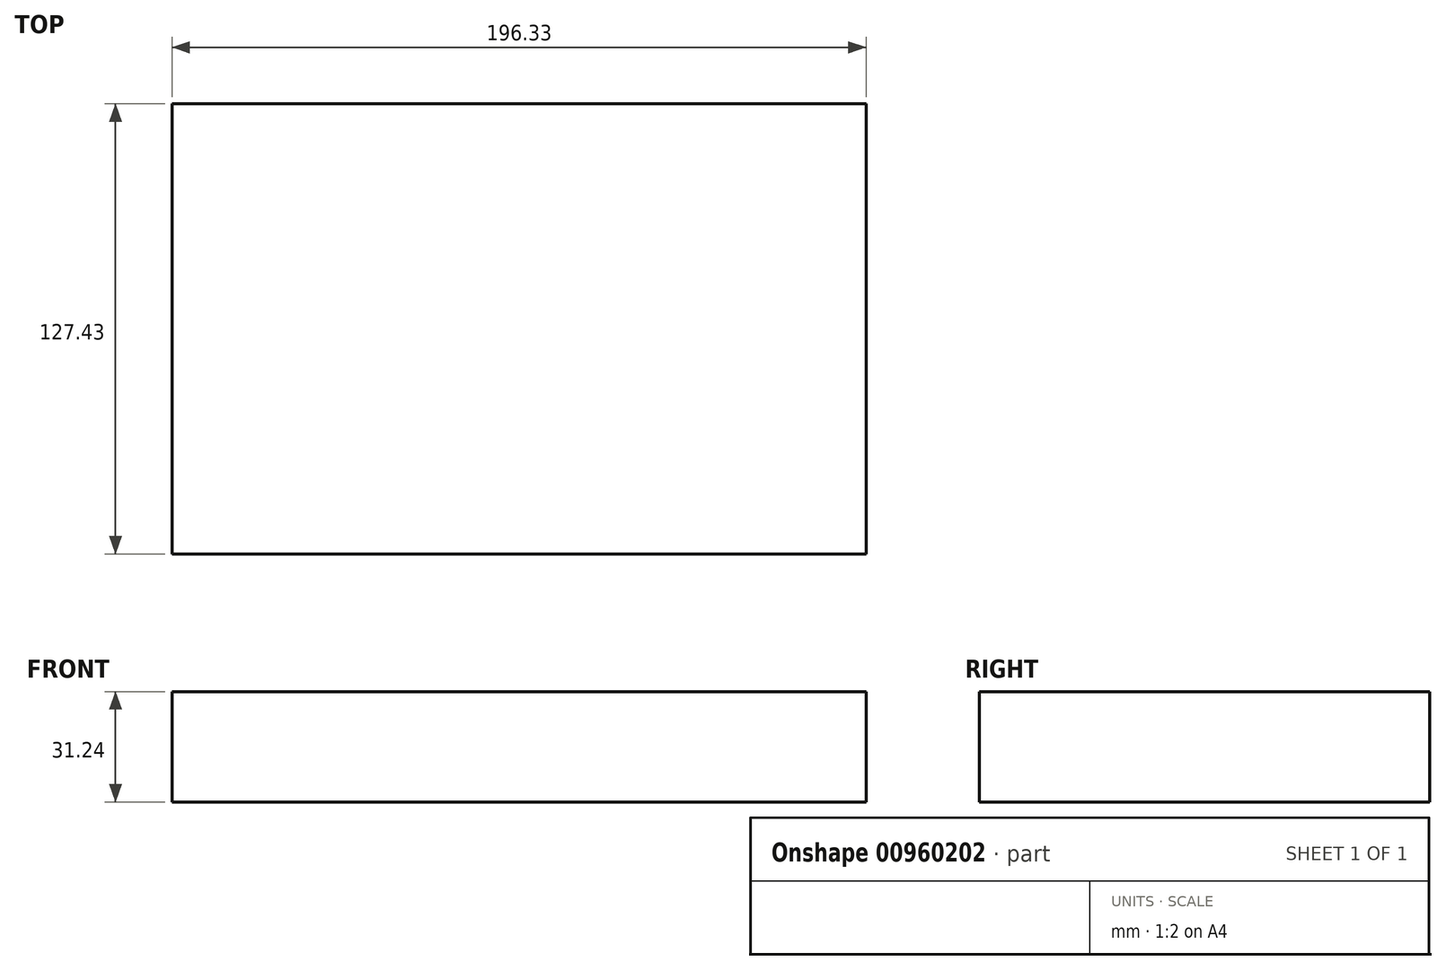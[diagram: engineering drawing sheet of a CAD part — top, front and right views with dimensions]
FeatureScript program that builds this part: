
annotation { "Feature Type Name" : "Feature", "Feature Type Description" : "" }
export const myFeature = defineFeature(function(context is Context, id is Id, definition is map)
    precondition{}
    {
        {
            var Q0;
            Q0=qCreatedBy(makeId("Top.planeOp"),FACE);
            var sketch = newSketch(context, id + "F0", { "sketchPlane" : qUnion([Q0])});
            skLineSegment(sketch, "E0.bottom", {"start": v(-95.8, 66.26) * mm, "end": v(100.53, 66.26) * mm});
            skLineSegment(sketch, "E0.top", {"start": v(-95.8, -61.17) * mm, "end": v(100.53, -61.17) * mm});
            skLineSegment(sketch, "E0.left", {"start": v(-95.8, 66.26) * mm, "end": v(-95.8, -61.17) * mm});
            skLineSegment(sketch, "E0.right", {"start": v(100.53, 66.26) * mm, "end": v(100.53, -61.17) * mm});
            skSolve(sketch);
        }
        {
            var Q0;
            Q0=makeQuery(id+"F0.imprint","IMPRINT",FACE,{"disambiguationData":[TD([[makeQuery(id+"F0.imprint","IMPRINT",EDGE,{"derivedFrom":sQuery(id+"F0.wireOp",EDGE,"E0.bottom")}),-1.0]])]});
            extrude(context, id + "F1", {"entities" : qUnion([Q0]), "depth" : 31.24 * mm, "offsetDistance" : 25.4 * mm});
        }
        {
            var Q0;
            Q0=makeQuery(id+"F1.opExtrude","SWEPT_FACE",FACE,{"disambiguationData":[OSD([sQuery(id+"F0.wireOp",EDGE,"E0.top")])]});
            var sketch = newSketch(context, id + "F2", { "sketchPlane" : qUnion([Q0])});
            skCircle(sketch, "E1", {"center": v(55.6, 14.95) * mm, "radius": 7.16 * mm});
            skSolve(sketch);
        }
        {
            var Q0;
            Q0=sQuery(id+"F2.wireOp",VERTEX,"E1.center");
            var Q1;
            Q1=makeQuery(id+"F1.opExtrude","SWEPT_BODY",BODY,{"disambiguationData":[OSD([sQuery(id+"F0.wireOp",EDGE,"E0.bottom"),sQuery(id+"F0.wireOp",EDGE,"E0.top"),sQuery(id+"F0.wireOp",EDGE,"E0.left"),sQuery(id+"F0.wireOp",EDGE,"E0.right")])]});
            hole(context, id + "F3", {"style" : HoleStyle.SIMPLE, "endStyle" : HoleEndStyle.BLIND, "holeDiameter" : 7.62 * mm, "majorDiameter" : 6.35 * mm, "holeDepth" : 127 * mm, "isTappedThrough" : true, "tappedDepth" : 12.7 * mm, "tapClearance" : 3, "locations" : qUnion([Q0]), "scope" : qUnion([Q1])});
        }
        {
            var Q0;
            Q0=makeQuery(id+"F1.opExtrude","CAP_FACE",FACE,{"disambiguationData":[OSD([sQuery(id+"F0.wireOp",EDGE,"E0.bottom"),sQuery(id+"F0.wireOp",EDGE,"E0.top"),sQuery(id+"F0.wireOp",EDGE,"E0.left"),sQuery(id+"F0.wireOp",EDGE,"E0.right")])],"isStart":false});
            extrude(context, id + "F4", {"entities" : qUnion([Q0]), "operationType" : NewBodyOperationType.ADD, "oppositeDirection" : true, "depth" : 22.86 * mm, "offsetDistance" : 25.4 * mm});
        }
    });
